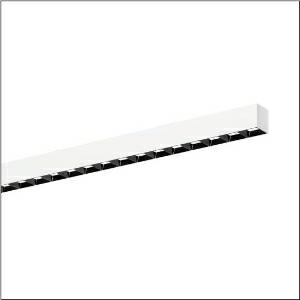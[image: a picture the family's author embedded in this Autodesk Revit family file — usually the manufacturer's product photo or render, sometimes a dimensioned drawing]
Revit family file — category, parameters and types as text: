
# Revit family: silica_r__21_51mx24dk36wb_35db
name_source: partatom
category: Lighting Fixtures
units: mm (PartAtom-declared; Revit-internal decimal feet)

## family parameters
Cut with Voids When Loaded = No
Host = Face
Light Source = No
Part Type = Normal
Room Calculation Point = No
Round Connector Dimension = Use Diameter
Shared = No

## types (1)
- --- (1 x LED, 6480 lm, 48.2 W, 3000K)
    Apparent Load = 48 VA
    CIE Flux Codes = 74 94 99 100 100
    Color Rendering = 80
    Color Temperature = 3000K
    Default Elevation = 1800 mm
    Description = Silica® 21, office luminaire, primary light control with darklight reflector, of PMMA, black, CAT 2 (L<= 3000cd/m²), light emission: direct distribution, primary light characteristic: symmetric, installation type: surface-mounted, LED, rated luminous flux: 6.480lm, luminous efficacy: 134lm/W, light colour: 830, colour temperature: 3000K, control gear: DALI 2, with terminal, 3+2-pole, max. 2.5mm², mains connection: 220..240V, AC, 50/60Hz, rated input power: 48.2W, luminaire housing, of aluminium, traffic white (RAL 9016), length: 1.800mm, width: 53mm, height: 53mm, protection rating (complete): IP20, insulation class (complete): insulation class I (protective earthing), certification: CE, permissible operating ambient temperature: 0..+35°C, standard: EN 50419, packaging unit: 1 piece
    Height = 53 mm
    Lamp = 1 x LED
    Lamp Light Flux = 6480 lm
    Lamp Power = 48.2 W
    Lamp count = 1
    Length = 1804 mm
    Luminous efficacy = 134 lm/W
    Manufacturer = Siteco
    ModVariant = No
    Model = 51MX24DK36WB
    Mounting Place = Ceiling
    Mounting Type = Surface mounted
    Number of Poles = 1
    OnlyDefault = Yes
    Power Factor = 1
    Product Name = Silica® 21
    Product group = office luminaire | ceiling mounted
    ProductGroupID = 303
    Protection Class = Protection class I
    Protection Degree = IP 20
    RLX_Detail_Level = 1
    RLX_Emergency_Light_Flux = 0 lm
    RLX_Emergency_Type = 0
    RLX_Emergency_Type_DB = No
    RlxData = <blob elided: 32385 chars, md5=39e5cfbf>
    Socket = socket
    Standby Power = 0 W
    System Light Flux = 6480 lm
    System Power = 48 W
    Type Comments = factory setting: luminous flux: 100 % | dim-lin: 254 | 447 mA
    Type Image = l_1335873.jpg
    URL = http://relux.com
    VarID = @adj_090363
    Voltage = 0 V
    Weight = 0.00 kg
    Width = 53 mm

## geometry (parser evidence)
native form markers: Blend x4, Sweep x10
no freeform markers — native parametric forms only
